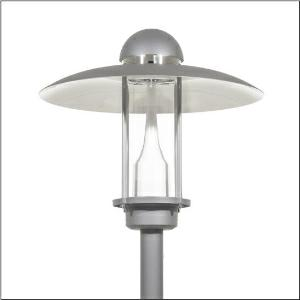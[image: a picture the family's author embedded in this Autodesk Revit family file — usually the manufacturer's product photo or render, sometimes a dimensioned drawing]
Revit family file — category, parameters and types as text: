
# Revit family: city-light_elegance_iq___st1_2a_5xa5265mf14h_1b27
name_source: partatom
category: Lighting Fixtures
units: mm (PartAtom-declared; Revit-internal decimal feet)

## family parameters
Cut with Voids When Loaded = No
Host = Face
Light Source = No
Part Type = Normal
Room Calculation Point = No
Round Connector Dimension = Use Diameter
Shared = No

## types (1)
- --- (1 x LED, 1470 lm, 11.8 W, 2700K)
    Apparent Load = 12 VA
    CIE Flux Codes = 22 62 94 98 100
    Color Rendering = 70
    Color Temperature = 2700K
    Default Elevation = 1800 mm
    Description = City-Light Elegance iQ, mast luminaire, Module 540 iQ-SR, primary light control with 3 zone facetted reflector, of plastic, silver coated, highly specular, structured, primary optical cover: cover, of PMMA, transparent, light distribution: ST1.2a, light emission: direct distribution, primary light characteristic: asymmetric, installation type: post-top, LED, High Power LED, rated luminous flux: 1.470lm, luminous efficacy: 124lm/W, light colour: 727, colour temperature: 2700K, control gear: ECG iQ, control: pre-setting: logarithmic dimming characteristic, Street-Remote, Auto-Match, Temp-Guard, Lumen-Switch, Night-Set, Smart-Wire, Light-Fading, Desk-Remote (wireless, voltage-free reading and setting of iQ features in the workshop via application-optimized NFC function/RFID function), optimised constant luminous flux control (CLO 2.0), with terminal, 6-pole, max. 2.5mm², mains connection: 230..240V, AC, 50/60Hz, start of lifetime: 12W, end of service life: 12W, reduction: 6W, luminaire housing, upper part, of aluminium, coated, Siteco® metallic grey (DB 702S), diameter: 750mm, height: 675mm, spigot size: d x l = 76 x 70mm (post-top) | with reducer (optional accessory) 60 x 70mm, post-top mast mounting element, of diecast aluminium, coated, Siteco® metallic grey (DB 702S), Module 540 iQ-SR, traffic white (RAL 9016), equipment: standard, protection rating (complete): IP65, insulation class (complete): insulation class II (safety insulation), certification: CE, ENEC, VDE, packaging unit: 1 piece

Light Distribution: ST1.2a
    Height = 675 mm
    Lamp = 1 x LED
    Lamp Light Flux = 1470 lm
    Lamp Power = 11.8 W
    Lamp count = 1
    Length = 750 mm
    Luminous efficacy = 125 lm/W
    Manufacturer = Siteco
    ModVariant = No
    Model = 5XA5265MF14H
    Number of Poles = 1
    OnlyDefault = Yes
    Power Factor = 1
    Product Name = City-Light Elegance iQ | ST1.2a
    Product group = mast luminaire | pylon top
    ProductGroupID = 6100
    Protection Class = Protection class II
    Protection Degree = IP 65
    RLX_Detail_Level = 1
    RLX_Emergency_Light_Flux = 0 lm
    RLX_Emergency_Type = 0
    RLX_Emergency_Type_DB = No
    RlxData = <blob elided: 99609 chars, md5=29b64e6f>
    Socket = socket
    Standby Power = 0 W
    System Light Flux = 1470 lm
    System Power = 12 W
    Type Comments = factory setting: luminous flux: 100 % | dim-lin: 254 | 472 mA
    Type Image = l_1006912.jpg
    URL = http://relux.com
    VarID = @adj_123619
    Voltage = 0 V
    Weight = 0.00 kg
    Width = 0 mm  [stored 0 ft]

note: [stored X ft] marks values corroborated as IEEE doubles in the binary element streams (Revit-internal decimal feet)

## geometry (parser evidence)
native form markers: Blend x4, Sweep x10
no freeform markers — native parametric forms only
